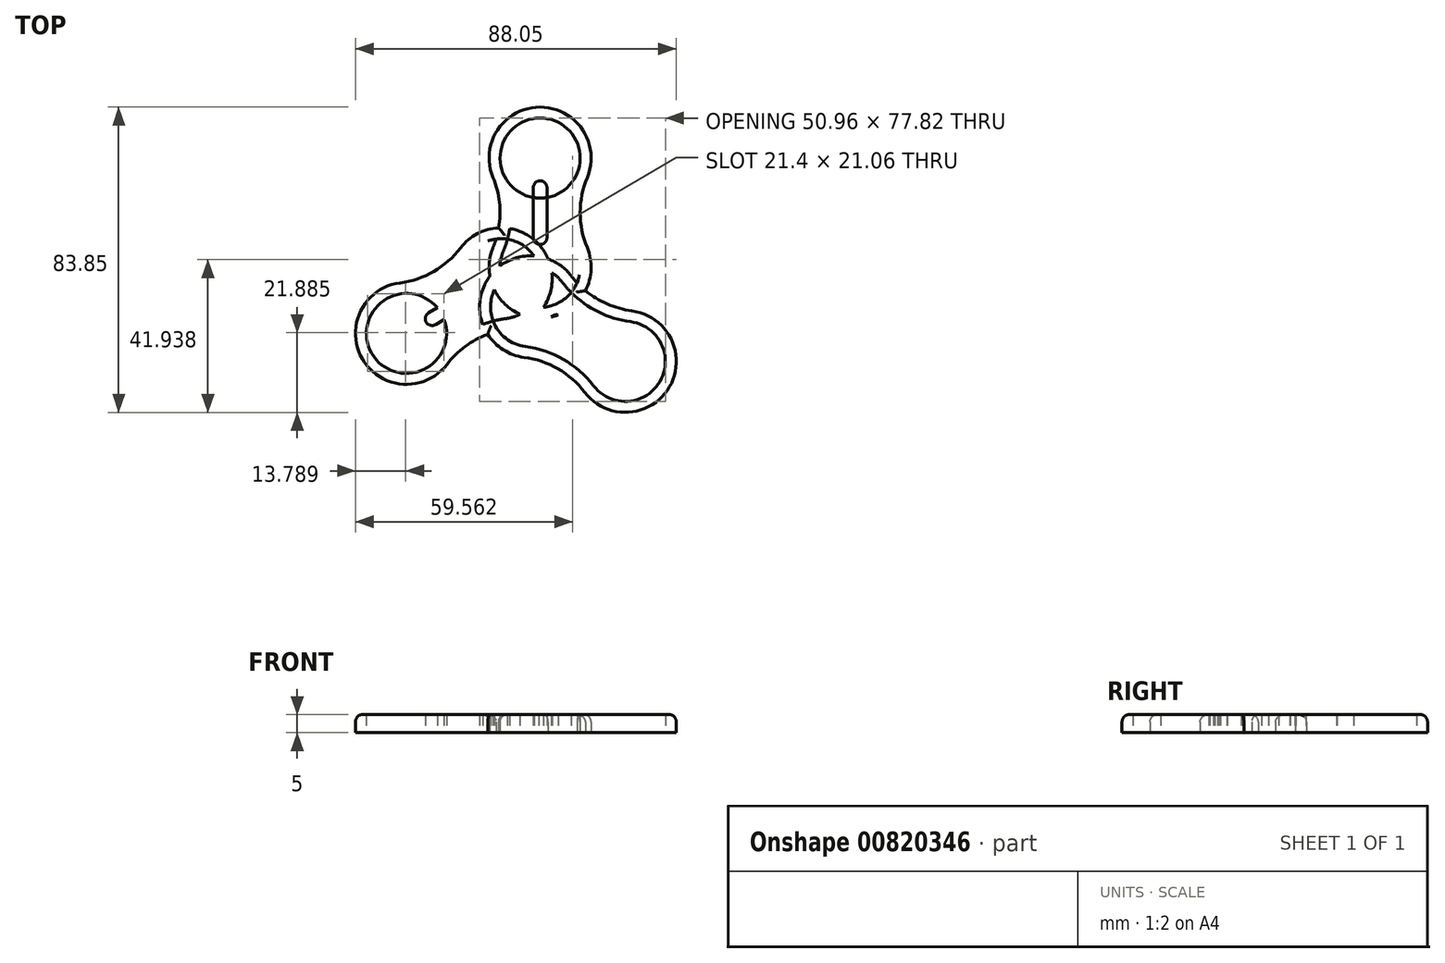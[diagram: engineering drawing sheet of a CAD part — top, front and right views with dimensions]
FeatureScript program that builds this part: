
annotation { "Feature Type Name" : "Feature", "Feature Type Description" : "" }
export const myFeature = defineFeature(function(context is Context, id is Id, definition is map)
    precondition{}
    {
        {
            var Q0;
            Q0=qCreatedBy(makeId("Top.planeOp"),FACE);
            var sketch = newSketch(context, id + "F0", { "sketchPlane" : qUnion([Q0])});
            skArc(sketch, "E0", {"start": v(-10.15, 4.23) * mm, "mid": v(0, -11) * mm, "end": v(10.15, 4.23) * mm});
            skArc(sketch, "E1", {"start": v(10.15, 25.77) * mm, "mid": v(0, 41) * mm, "end": v(-10.15, 25.77) * mm});
            skArc(sketch, "E2", {"start": v(-10.15, 4.23) * mm, "mid": v(-8, 15) * mm, "end": v(-10.15, 25.77) * mm});
            skArc(sketch, "E3", {"start": v(10.15, 25.77) * mm, "mid": v(8, 15) * mm, "end": v(10.15, 4.23) * mm});
            skLineSegment(sketch, "E4.left", {"start": v(1.88, 8.13) * mm, "end": v(1.88, 21.87) * mm});
            skLineSegment(sketch, "E4.right", {"start": v(-1.88, 8.13) * mm, "end": v(-1.88, 21.87) * mm});
            skPoint(sketch, "E4.middle", {"position": v(0, 15) * mm});
            skPoint(sketch, "E4.middle.positionSnap0", {"position": v(-8, 15) * mm});
            skPoint(sketch, "E4.centerSnap0", {"position": v(-8, 15) * mm});
            skArc(sketch, "E5", {"start": v(-1.88, 8.13) * mm, "mid": v(0, 6.25) * mm, "end": v(1.88, 8.13) * mm});
            skArc(sketch, "E6", {"start": v(1.88, 21.87) * mm, "mid": v(0, 23.75) * mm, "end": v(-1.88, 21.87) * mm});
            skArc(sketch, "E7.0", {"start": v(12.92, 24.62) * mm, "mid": v(0, 44) * mm, "end": v(-12.92, 24.62) * mm});
            skArc(sketch, "E7.1", {"start": v(12.92, 24.62) * mm, "mid": v(11, 15) * mm, "end": v(12.92, 5.38) * mm});
            skArc(sketch, "E7.2", {"start": v(-12.92, 5.38) * mm, "mid": v(0, -14) * mm, "end": v(12.92, 5.38) * mm});
            skArc(sketch, "E7.3", {"start": v(-12.92, 5.38) * mm, "mid": v(-11, 15) * mm, "end": v(-12.92, 24.62) * mm});
            skCircle(sketch, "E8", {"center": v(0, 30) * mm, "radius": 11 * mm});
            skArc(sketch, "E9.1.0", {"start": v(-38.47, -4.29) * mm, "mid": v(-48.8, -25.17) * mm, "end": v(-25.55, -26.67) * mm});
            skArc(sketch, "E9.1.1", {"start": v(-38.47, -4.29) * mm, "mid": v(-29.18, -1.14) * mm, "end": v(-21.82, 5.33) * mm});
            skArc(sketch, "E9.1.2", {"start": v(-8.9, -17.05) * mm, "mid": v(1.43, 3.83) * mm, "end": v(-21.82, 5.33) * mm});
            skArc(sketch, "E9.1.3", {"start": v(-9.28, -14.08) * mm, "mid": v(-1.17, 2.33) * mm, "end": v(-19.43, 3.5) * mm});
            skArc(sketch, "E9.1.4", {"start": v(-8.9, -17.05) * mm, "mid": v(-18.18, -20.2) * mm, "end": v(-25.55, -26.67) * mm});
            skArc(sketch, "E9.1.5", {"start": v(-9.28, -14.08) * mm, "mid": v(-19.68, -17.6) * mm, "end": v(-27.93, -24.85) * mm});
            skCircle(sketch, "E9.1.6", {"center": v(-36.67, -18.17) * mm, "radius": 11 * mm});
            skArc(sketch, "E9.1.7", {"start": v(-38.09, -7.26) * mm, "mid": v(-27.68, -3.74) * mm, "end": v(-19.43, 3.5) * mm});
            skLineSegment(sketch, "E9.1.8", {"start": v(-18.67, -5.6) * mm, "end": v(-30.57, -12.48) * mm});
            skLineSegment(sketch, "E9.1.9", {"start": v(-16.8, -8.86) * mm, "end": v(-28.7, -15.73) * mm});
            skArc(sketch, "E9.1.10", {"start": v(-16.8, -8.86) * mm, "mid": v(-16.1, -6.3) * mm, "end": v(-18.67, -5.6) * mm});
            skArc(sketch, "E9.1.11", {"start": v(-30.57, -12.48) * mm, "mid": v(-31.26, -15.04) * mm, "end": v(-28.7, -15.73) * mm});
            skArc(sketch, "E9.2.0", {"start": v(12.25, -34.35) * mm, "mid": v(35.5, -32.85) * mm, "end": v(25.18, -11.96) * mm});
            skArc(sketch, "E9.2.1", {"start": v(12.25, -34.35) * mm, "mid": v(4.89, -27.87) * mm, "end": v(-4.4, -24.73) * mm});
            skArc(sketch, "E9.2.2", {"start": v(8.52, -2.35) * mm, "mid": v(-14.73, -3.85) * mm, "end": v(-4.4, -24.73) * mm});
            skArc(sketch, "E9.2.3", {"start": v(6.14, -4.17) * mm, "mid": v(-12.13, -5.35) * mm, "end": v(-4.01, -21.75) * mm});
            skArc(sketch, "E9.2.4", {"start": v(8.52, -2.35) * mm, "mid": v(15.89, -8.82) * mm, "end": v(25.18, -11.96) * mm});
            skArc(sketch, "E9.2.5", {"start": v(6.14, -4.17) * mm, "mid": v(14.39, -11.42) * mm, "end": v(24.8, -14.94) * mm});
            skCircle(sketch, "E9.2.6", {"center": v(23.38, -25.85) * mm, "radius": 11 * mm});
            skArc(sketch, "E9.2.7", {"start": v(14.64, -32.52) * mm, "mid": v(6.39, -25.27) * mm, "end": v(-4.01, -21.75) * mm});
            skLineSegment(sketch, "E9.2.8", {"start": v(3.5, -16.54) * mm, "end": v(15.4, -23.4) * mm});
            skLineSegment(sketch, "E9.2.9", {"start": v(5.38, -13.28) * mm, "end": v(17.28, -20.15) * mm});
            skArc(sketch, "E9.2.10", {"start": v(5.38, -13.28) * mm, "mid": v(2.81, -13.97) * mm, "end": v(3.5, -16.54) * mm});
            skArc(sketch, "E9.2.11", {"start": v(15.4, -23.4) * mm, "mid": v(17.96, -22.72) * mm, "end": v(17.28, -20.15) * mm});
            skPoint(sketch, "E9.center", {"position": v(-4.43, -4.67) * mm});
            skSolve(sketch);
        }
        {
            var Q0;
            Q0 = qSketchRegion(id + "F0", true);
            var Q1;
            {var subQ2=sQuery(id+"F0.wireOp",EDGE,"E2");var subQ5=sQuery(id+"F0.wireOp",EDGE,"E9.1.7");var subQ6=makeQuery(id+"F0.imprint","INTERSECT",VERTEX,{"derivedFrom":[subQ2,subQ5]});Q1=makeQuery(id+"F0.imprint","IMPRINT",FACE,{"disambiguationData":[TD([[makeQuery(id+"F0.imprint","IMPRINT",EDGE,{"disambiguationData":[TD([[subQ6,-1.0]])],"derivedFrom":subQ2}),1.0]])]});}
            var Q2;
            {var subQ4=sQuery(id+"F0.wireOp",EDGE,"E9.2.2");var subQ6=sQuery(id+"F0.wireOp",EDGE,"E3");var subQ7=makeQuery(id+"F0.imprint","INTERSECT",VERTEX,{"derivedFrom":[subQ6,subQ4]});Q2=makeQuery(id+"F0.imprint","IMPRINT",FACE,{"disambiguationData":[TD([[makeQuery(id+"F0.imprint","IMPRINT",EDGE,{"disambiguationData":[TD([[subQ7,-1.0]])],"derivedFrom":subQ6}),1.0]])]});}
            var Q3;
            {var subQ5=sQuery(id+"F0.wireOp",EDGE,"E7.2");Q3=makeQuery(id+"F0.imprint","IMPRINT",FACE,{"disambiguationData":[TD([[makeQuery(id+"F0.imprint","IMPRINT",EDGE,{"derivedFrom":subQ5}),1.0]])]});}
            var Q4;
            {var subQ0=sQuery(id+"F0.wireOp",EDGE,"E9.1.6");var subQ1=sQuery(id+"F0.wireOp",EDGE,"E9.1.5");var subQ2=makeQuery(id+"F0.imprint","INTERSECT",VERTEX,{"derivedFrom":[subQ1,subQ0]});Q4=makeQuery(id+"F0.imprint","IMPRINT",FACE,{"disambiguationData":[TD([[makeQuery(id+"F0.imprint","IMPRINT",EDGE,{"disambiguationData":[TD([[subQ2,1.0]])],"derivedFrom":subQ1}),-1.0]])]});}
            var Q5;
            {var subQ0=sQuery(id+"F0.wireOp",EDGE,"E9.1.7");var subQ1=sQuery(id+"F0.wireOp",EDGE,"E9.1.6");var subQ2=makeQuery(id+"F0.imprint","INTERSECT",VERTEX,{"derivedFrom":[subQ1,subQ0]});Q5=makeQuery(id+"F0.imprint","IMPRINT",FACE,{"disambiguationData":[TD([[makeQuery(id+"F0.imprint","IMPRINT",EDGE,{"disambiguationData":[TD([[subQ2,1.0]])],"derivedFrom":subQ1}),-1.0]])]});}
            var Q6;
            {var subQ0=sQuery(id+"F0.wireOp",EDGE,"E8");var subQ1=sQuery(id+"F0.wireOp",EDGE,"E3");var subQ2=makeQuery(id+"F0.imprint","INTERSECT",VERTEX,{"derivedFrom":[subQ1,subQ0]});Q6=makeQuery(id+"F0.imprint","IMPRINT",FACE,{"disambiguationData":[TD([[makeQuery(id+"F0.imprint","IMPRINT",EDGE,{"disambiguationData":[TD([[subQ2,-1.0]])],"derivedFrom":subQ1}),-1.0]])]});}
            var Q7;
            {var subQ0=sQuery(id+"F0.wireOp",EDGE,"E8");var subQ1=sQuery(id+"F0.wireOp",EDGE,"E2");var subQ2=makeQuery(id+"F0.imprint","INTERSECT",VERTEX,{"derivedFrom":[subQ1,subQ0]});Q7=makeQuery(id+"F0.imprint","IMPRINT",FACE,{"disambiguationData":[TD([[makeQuery(id+"F0.imprint","IMPRINT",EDGE,{"disambiguationData":[TD([[subQ2,1.0]])],"derivedFrom":subQ1}),-1.0]])]});}
            var Q8;
            {var subQ5=sQuery(id+"F0.wireOp",EDGE,"E2");var subQ7=sQuery(id+"F0.wireOp",EDGE,"E9.2.3");var subQ9=makeQuery(id+"F0.imprint","INTERSECT",VERTEX,{"derivedFrom":[subQ5,subQ7]});Q8=makeQuery(id+"F0.imprint","IMPRINT",FACE,{"disambiguationData":[TD([[makeQuery(id+"F0.imprint","IMPRINT",EDGE,{"disambiguationData":[TD([[subQ9,-1.0]])],"derivedFrom":subQ5}),1.0]])]});}
            var Q9;
            {var subQ1=sQuery(id+"F0.wireOp",EDGE,"E9.1.5");var subQ5=sQuery(id+"F0.wireOp",EDGE,"E9.2.7");var subQ9=makeQuery(id+"F0.imprint","INTERSECT",VERTEX,{"derivedFrom":[subQ1,subQ5]});Q9=makeQuery(id+"F0.imprint","IMPRINT",FACE,{"disambiguationData":[TD([[makeQuery(id+"F0.imprint","IMPRINT",EDGE,{"disambiguationData":[TD([[subQ9,-1.0]])],"derivedFrom":subQ1}),-1.0]])]});}
            var Q10;
            {var subQ0=sQuery(id+"F0.wireOp",EDGE,"E9.1.3");var subQ1=sQuery(id+"F0.wireOp",EDGE,"E3");var subQ2=makeQuery(id+"F0.imprint","INTERSECT",VERTEX,{"derivedFrom":[subQ1,subQ0]});Q10=makeQuery(id+"F0.imprint","IMPRINT",FACE,{"disambiguationData":[TD([[makeQuery(id+"F0.imprint","IMPRINT",EDGE,{"disambiguationData":[TD([[subQ2,1.0]])],"derivedFrom":subQ1}),1.0]])]});}
            var Q11;
            {var subQ0=sQuery(id+"F0.wireOp",EDGE,"E9.2.7");var subQ1=sQuery(id+"F0.wireOp",EDGE,"E9.1.2");var subQ2=makeQuery(id+"F0.imprint","INTERSECT",VERTEX,{"derivedFrom":[subQ1,subQ0]});Q11=makeQuery(id+"F0.imprint","IMPRINT",FACE,{"disambiguationData":[TD([[makeQuery(id+"F0.imprint","IMPRINT",EDGE,{"disambiguationData":[TD([[subQ2,-1.0]])],"derivedFrom":subQ1}),1.0]])]});}
            var Q12;
            {var subQ0=sQuery(id+"F0.wireOp",EDGE,"E9.2.7");var subQ1=sQuery(id+"F0.wireOp",EDGE,"E9.1.2");var subQ2=makeQuery(id+"F0.imprint","INTERSECT",VERTEX,{"derivedFrom":[subQ1,subQ0]});Q12=makeQuery(id+"F0.imprint","IMPRINT",FACE,{"disambiguationData":[TD([[makeQuery(id+"F0.imprint","IMPRINT",EDGE,{"disambiguationData":[TD([[subQ2,-1.0]])],"derivedFrom":subQ1}),-1.0]])]});}
            var Q13;
            {var subQ0=sQuery(id+"F0.wireOp",EDGE,"E9.2.9");var subQ1=sQuery(id+"F0.wireOp",EDGE,"E9.1.2");var subQ2=makeQuery(id+"F0.imprint","INTERSECT",VERTEX,{"derivedFrom":[subQ1,subQ0]});Q13=makeQuery(id+"F0.imprint","IMPRINT",FACE,{"disambiguationData":[TD([[makeQuery(id+"F0.imprint","IMPRINT",EDGE,{"disambiguationData":[TD([[subQ2,-1.0]])],"derivedFrom":subQ1}),-1.0]])]});}
            var Q14;
            {var subQ5=sQuery(id+"F0.wireOp",EDGE,"E9.2.2");var subQ6=sQuery(id+"F0.wireOp",EDGE,"E3");var subQ7=makeQuery(id+"F0.imprint","INTERSECT",VERTEX,{"derivedFrom":[subQ6,subQ5]});Q14=makeQuery(id+"F0.imprint","IMPRINT",FACE,{"disambiguationData":[TD([[makeQuery(id+"F0.imprint","IMPRINT",EDGE,{"disambiguationData":[TD([[subQ7,-1.0]])],"derivedFrom":subQ6}),-1.0]])]});}
            var Q15;
            {var subQ1=sQuery(id+"F0.wireOp",EDGE,"E2");var subQ5=sQuery(id+"F0.wireOp",EDGE,"E9.1.7");var subQ6=makeQuery(id+"F0.imprint","INTERSECT",VERTEX,{"derivedFrom":[subQ1,subQ5]});Q15=makeQuery(id+"F0.imprint","IMPRINT",FACE,{"disambiguationData":[TD([[makeQuery(id+"F0.imprint","IMPRINT",EDGE,{"disambiguationData":[TD([[subQ6,-1.0]])],"derivedFrom":subQ1}),-1.0]])]});}
            var Q16;
            {var subQ0=sQuery(id+"F0.wireOp",EDGE,"E9.1.9");var subQ1=sQuery(id+"F0.wireOp",EDGE,"E9.1.6");var subQ2=makeQuery(id+"F0.imprint","INTERSECT",VERTEX,{"derivedFrom":[subQ1,subQ0]});Q16=makeQuery(id+"F0.imprint","IMPRINT",FACE,{"disambiguationData":[TD([[makeQuery(id+"F0.imprint","IMPRINT",EDGE,{"disambiguationData":[TD([[subQ2,-1.0]])],"derivedFrom":subQ1}),-1.0]])]});}
            var Q17;
            {var subQ0=sQuery(id+"F0.wireOp",EDGE,"E9.2.3");var subQ1=sQuery(id+"F0.wireOp",EDGE,"E9.1.8");var subQ2=makeQuery(id+"F0.imprint","INTERSECT",VERTEX,{"derivedFrom":[subQ1,subQ0]});Q17=makeQuery(id+"F0.imprint","IMPRINT",FACE,{"disambiguationData":[TD([[makeQuery(id+"F0.imprint","IMPRINT",EDGE,{"disambiguationData":[TD([[subQ2,-1.0]])],"derivedFrom":subQ1}),1.0]])]});}
            var Q18;
            {var subQ0=sQuery(id+"F0.wireOp",EDGE,"E9.2.8");var subQ1=sQuery(id+"F0.wireOp",EDGE,"E9.1.2");var subQ2=makeQuery(id+"F0.imprint","INTERSECT",VERTEX,{"derivedFrom":[subQ1,subQ0]});Q18=makeQuery(id+"F0.imprint","IMPRINT",FACE,{"disambiguationData":[TD([[makeQuery(id+"F0.imprint","IMPRINT",EDGE,{"disambiguationData":[TD([[subQ2,-1.0]])],"derivedFrom":subQ1}),1.0]])]});}
            var Q19;
            {var subQ0=sQuery(id+"F0.wireOp",EDGE,"E9.2.8");var subQ1=sQuery(id+"F0.wireOp",EDGE,"E9.1.2");var subQ2=makeQuery(id+"F0.imprint","INTERSECT",VERTEX,{"derivedFrom":[subQ1,subQ0]});Q19=makeQuery(id+"F0.imprint","IMPRINT",FACE,{"disambiguationData":[TD([[makeQuery(id+"F0.imprint","IMPRINT",EDGE,{"disambiguationData":[TD([[subQ2,-1.0]])],"derivedFrom":subQ1}),-1.0]])]});}
            var Q20;
            {var subQ0=sQuery(id+"F0.wireOp",EDGE,"E9.2.2");var subQ1=sQuery(id+"F0.wireOp",EDGE,"E4.left");var subQ2=makeQuery(id+"F0.imprint","INTERSECT",VERTEX,{"derivedFrom":[subQ1,subQ0]});Q20=makeQuery(id+"F0.imprint","IMPRINT",FACE,{"disambiguationData":[TD([[makeQuery(id+"F0.imprint","IMPRINT",EDGE,{"disambiguationData":[TD([[subQ2,-1.0]])],"derivedFrom":subQ1}),1.0]])]});}
            var Q21;
            {var subQ0=sQuery(id+"F0.wireOp",EDGE,"E9.2.3");var subQ1=sQuery(id+"F0.wireOp",EDGE,"E4.left");var subQ2=makeQuery(id+"F0.imprint","INTERSECT",VERTEX,{"derivedFrom":[subQ1,subQ0]});Q21=makeQuery(id+"F0.imprint","IMPRINT",FACE,{"disambiguationData":[TD([[makeQuery(id+"F0.imprint","IMPRINT",EDGE,{"disambiguationData":[TD([[subQ2,-1.0]])],"derivedFrom":subQ1}),1.0]])]});}
            extrude(context, id + "F1", {"entities" : qUnion([Q0, Q1, Q2, Q3, Q4, Q5, Q6, Q7, Q8, Q9, Q10, Q11, Q12, Q13, Q14, Q15, Q16, Q17, Q18, Q19, Q20, Q21]), "depth" : 5 * mm, "offsetDistance" : 25 * mm});
        }
        {
            var Q0;
            Q0=makeQuery(id+"F1.opExtrude","CAP_EDGE",EDGE,{"disambiguationData":[OSD([sQuery(id+"F0.wireOp",EDGE,"E7.1")])],"isStart":false});
            var Q1;
            Q1=makeQuery(id+"F1.opExtrude","CAP_EDGE",EDGE,{"disambiguationData":[OSD([sQuery(id+"F0.wireOp",EDGE,"E9.2.4")])],"isStart":false});
            var Q2;
            Q2=makeQuery(id+"F1.opExtrude","CAP_EDGE",EDGE,{"disambiguationData":[OSD([sQuery(id+"F0.wireOp",EDGE,"E7.0")])],"isStart":false});
            var Q3;
            Q3=makeQuery(id+"F1.opExtrude","CAP_EDGE",EDGE,{"disambiguationData":[OSD([sQuery(id+"F0.wireOp",EDGE,"E7.3")])],"isStart":false});
            var Q4;
            Q4=makeQuery(id+"F1.opExtrude","CAP_EDGE",EDGE,{"disambiguationData":[OSD([sQuery(id+"F0.wireOp",EDGE,"E9.1.1")])],"isStart":false});
            var Q5;
            Q5=makeQuery(id+"F1.opExtrude","CAP_EDGE",EDGE,{"disambiguationData":[OSD([sQuery(id+"F0.wireOp",EDGE,"E9.1.0")])],"isStart":false});
            var Q6;
            Q6=makeQuery(id+"F1.opExtrude","CAP_EDGE",EDGE,{"disambiguationData":[OSD([sQuery(id+"F0.wireOp",EDGE,"E9.2.1")])],"isStart":false});
            var Q7;
            Q7=makeQuery(id+"F1.opExtrude","CAP_EDGE",EDGE,{"disambiguationData":[OSD([sQuery(id+"F0.wireOp",EDGE,"E9.1.4")])],"isStart":false});
            var Q8;
            Q8=makeQuery(id+"F1.opExtrude","CAP_EDGE",EDGE,{"disambiguationData":[OSD([sQuery(id+"F0.wireOp",EDGE,"E9.2.0")])],"isStart":false});
            fillet(context, id + "F2", {"entities" : qUnion([Q0, Q1, Q2, Q3, Q4, Q5, Q6, Q7, Q8]), "radius" : 2 * mm, "tangentPropagation" : true, "allowEdgeOverflow" : false});
        }
    });
